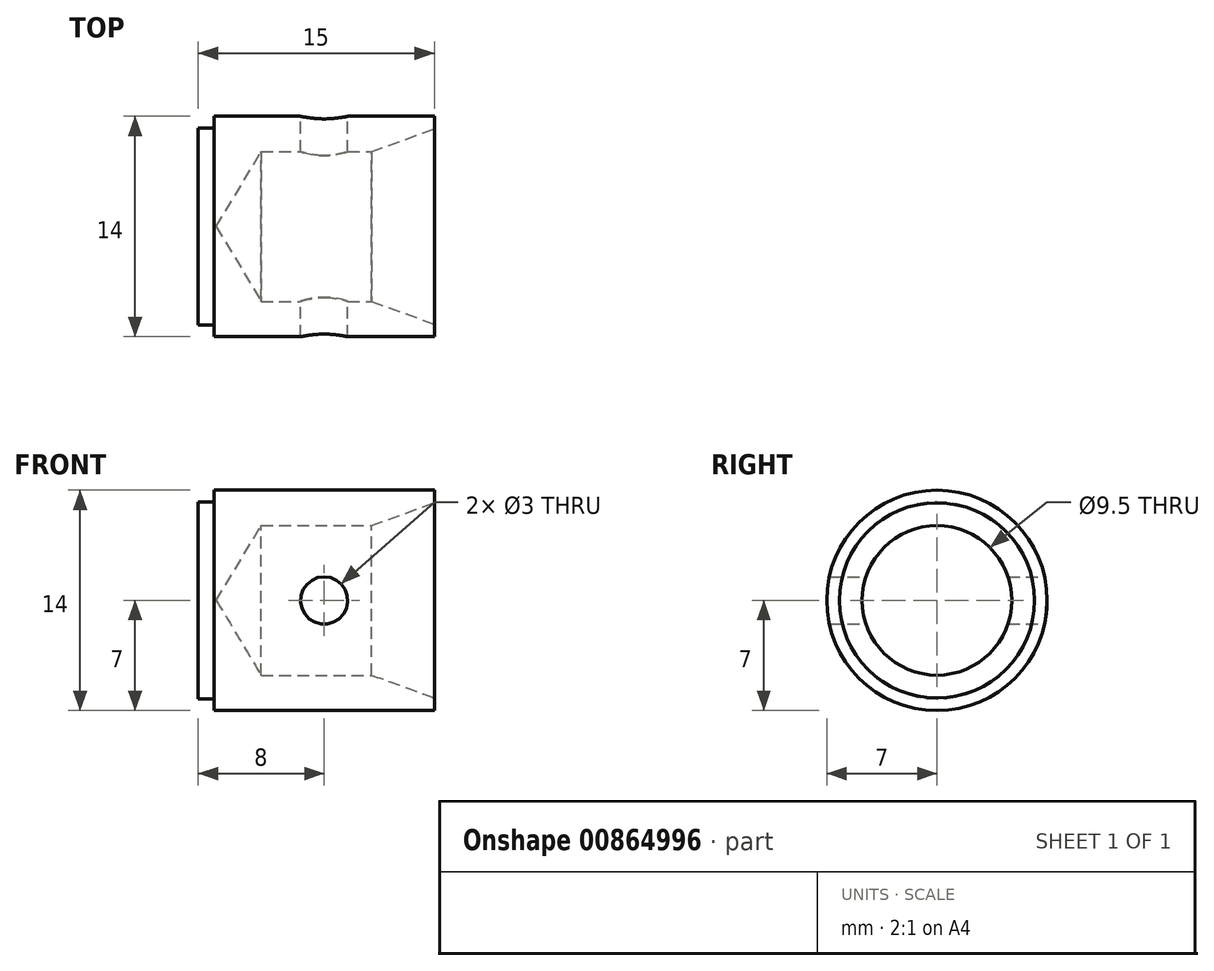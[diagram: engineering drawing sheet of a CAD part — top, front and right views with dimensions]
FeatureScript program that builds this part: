
annotation { "Feature Type Name" : "Feature", "Feature Type Description" : "" }
export const myFeature = defineFeature(function(context is Context, id is Id, definition is map)
    precondition{}
    {
        {
            var Q0;
            Q0=qCreatedBy(makeId("Front.planeOp"),FACE);
            var sketch = newSketch(context, id + "F0", { "sketchPlane" : qUnion([Q0])});
            skLineSegment(sketch, "E0", {"start": v(0, 0) * mm, "end": v(0, -6.25) * mm});
            skLineSegment(sketch, "E1", {"start": v(0, -6.25) * mm, "end": v(1, -6.25) * mm});
            skLineSegment(sketch, "E2", {"start": v(1, -6.25) * mm, "end": v(1, -7) * mm});
            skLineSegment(sketch, "E3", {"start": v(1, -7) * mm, "end": v(15, -7) * mm});
            skLineSegment(sketch, "E4", {"start": v(15, -7) * mm, "end": v(15, -6.2) * mm});
            skLineSegment(sketch, "E5", {"start": v(15, -6.2) * mm, "end": v(11.02, -4.75) * mm});
            skLineSegment(sketch, "E6", {"start": v(11.02, -4.75) * mm, "end": v(4, -4.75) * mm});
            skLineSegment(sketch, "E7", {"start": v(4, -4.75) * mm, "end": v(1.15, 0) * mm});
            skLineSegment(sketch, "E8", {"start": v(1.15, 0) * mm, "end": v(0, 0) * mm});
            skSolve(sketch);
        }
        {
            var Q0;
            Q0=makeQuery(id+"F0.imprint","IMPRINT",FACE,{"disambiguationData":[TD([[makeQuery(id+"F0.imprint","IMPRINT",EDGE,{"derivedFrom":sQuery(id+"F0.wireOp",EDGE,"E0")}),1.0]])]});
            var Q1;
            Q1=sQuery(id+"F0.wireOp",EDGE,"E8");
            revolve(context, id + "F1", {"surfaceOperationType" : NewSurfaceOperationType.NEW, "entities" : qUnion([Q0]), "axis" : qUnion([Q1]), "revolveType" : RevolveType.FULL});
        }
        {
            var Q0;
            Q0=qCreatedBy(makeId("Front.planeOp"),FACE);
            var sketch = newSketch(context, id + "F2", { "sketchPlane" : qUnion([Q0])});
            skCircle(sketch, "E9", {"center": v(8, 0) * mm, "radius": 1.5 * mm});
            skSolve(sketch);
        }
        {
            var Q0;
            Q0=makeQuery(id+"F2.imprint","IMPRINT",FACE,{"disambiguationData":[TD([[makeQuery(id+"F2.imprint","IMPRINT",EDGE,{"derivedFrom":sQuery(id+"F2.wireOp",EDGE,"E9")}),1.0]])]});
            extrude(context, id + "F3", {"entities" : qUnion([Q0]), "operationType" : NewBodyOperationType.REMOVE, "endBound" : BoundingType.SYMMETRIC, "depth" : 25 * mm, "offsetDistance" : 25 * mm});
        }
    });
